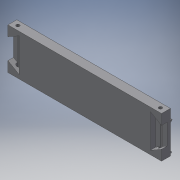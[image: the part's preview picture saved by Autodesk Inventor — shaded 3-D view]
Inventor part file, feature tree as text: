
AUTODESK INVENTOR PART (.ipt)
format: ipt  version: 2016 SP2 (Build 200236200, 236)  size: 220,160 bytes
history: native  units: mm
features: reference x17, extrude x7, sketch x7, mirror x1
ambient origin geometry x8: Origin, YZ Plane, XZ Plane, XY Plane, X Axis, Y Axis, Z Axis, Center Point
bodies: Volumenkörper1 (feature_tree)
feature tree (32):
  extrude  "Extrusion1"  Depth=0.1mm
  extrude  "Extrusion2"  Depth=35.0mm TaperAngle=0.0deg
  extrude  "Extrusion3"  Depth=1.0mm
  extrude  "Extrusion12"  Depth=1.0mm TaperAngle=0.0deg
  extrude  "Extrusion13"  Depth=12.55mm
  extrude  "Extrusion14"  Depth=5.0mm
  extrude  "Extrusion15"  Depth=2.2mm
  mirror  "Spiegeln3"
  sketch  "Skizze1"  dims[d0=69.4mm d1=0.0mm d7=0.1mm]
  reference  "Referenz1"
  reference  "Referenz2"
  reference  "Referenz3"
  reference  "Referenz4"
  reference  "Referenz5"
  reference  "Referenz6"
  reference  "Referenz8"
  reference  "Referenz9"
  sketch  "Skizze2"  dims[d8=5.0mm d9=0.0mm d10=35.0mm d11=0.0mm]
  sketch  "Skizze3"  dims[d19=2.0mm d20=1.0mm]
  reference  "Referenz10"
  reference  "Referenz11"
  reference  "Referenz12"
  reference  "Referenz13"
  reference  "Referenz14"
  sketch  "Skizze11"  dims[d21=1.0mm d51=4.45mm d52=0.0mm]
  reference  "Referenz19"
  reference  "Referenz20"
  reference  "Referenz21"
  reference  "Referenz22"
  sketch  "Skizze12"  dims[d53=19.4mm d54=12.55mm]
  sketch  "Skizze13"  dims[d55=10.0mm d56=5.0mm]
  sketch  "Skizze14"  dims[d57=36.75mm d58=0.0mm d59=3.1mm d60=5.0mm d61=5.0mm d62=5.0mm d63=0.0mm d64=5.7mm d65=2.2mm d66=0.0mm]
